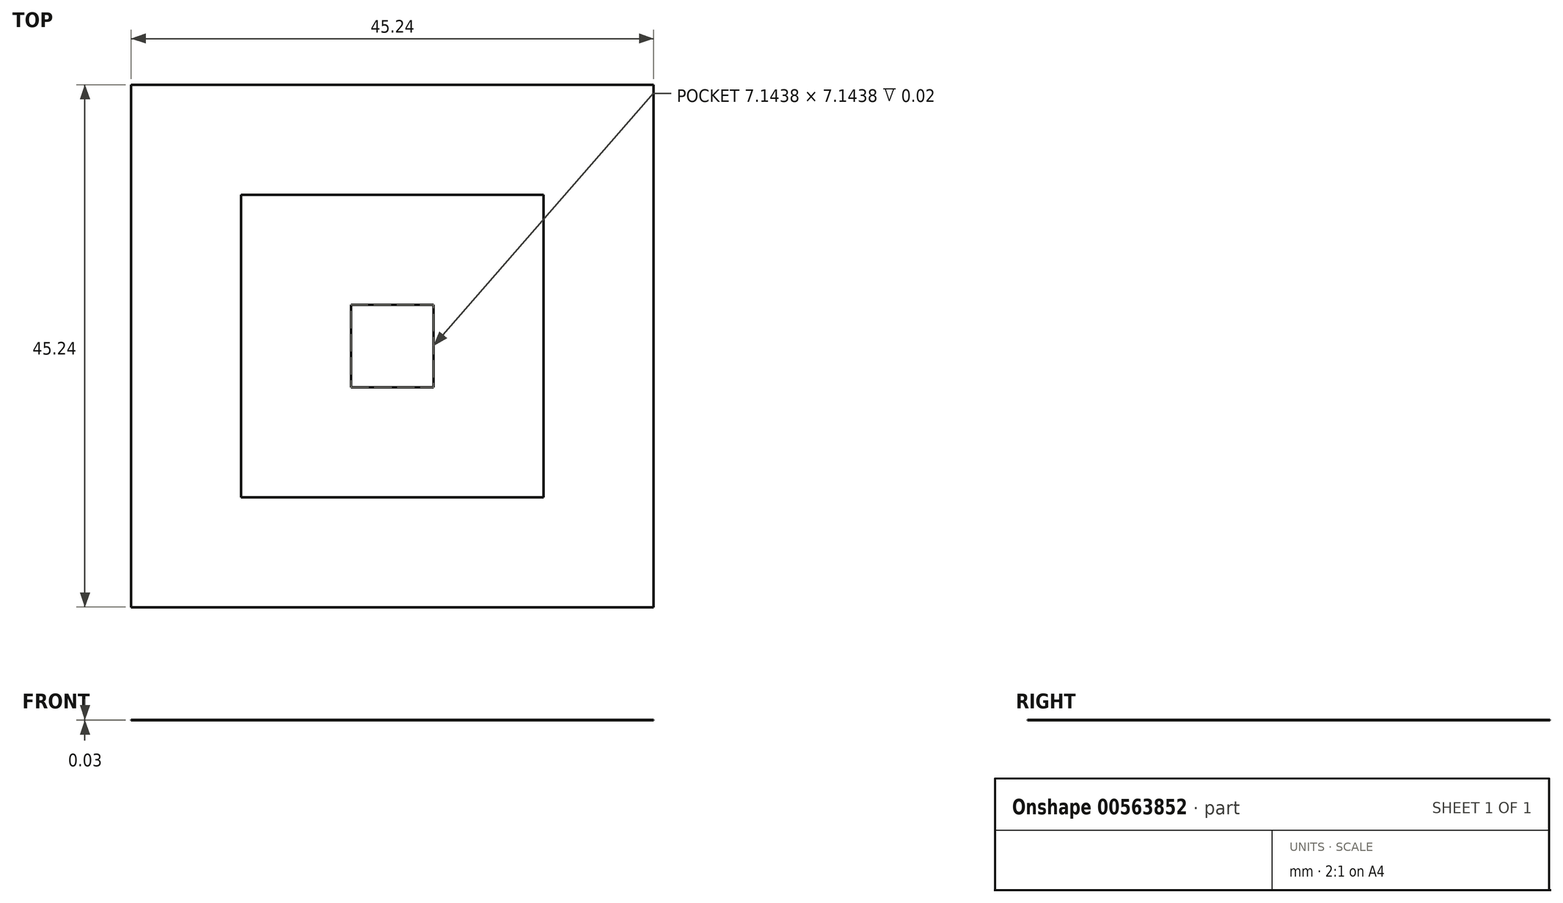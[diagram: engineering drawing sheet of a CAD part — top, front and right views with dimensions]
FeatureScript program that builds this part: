
annotation { "Feature Type Name" : "Feature", "Feature Type Description" : "" }
export const myFeature = defineFeature(function(context is Context, id is Id, definition is map)
    precondition{}
    {
        {
            var Q0;
            Q0=qCreatedBy(makeId("Top.planeOp"),FACE);
            var sketch = newSketch(context, id + "F0", { "sketchPlane" : qUnion([Q0])});
            skLineSegment(sketch, "E0.bottom", {"start": v(3.57, 3.57) * mm, "end": v(-3.57, 3.57) * mm});
            skLineSegment(sketch, "E0.top", {"start": v(3.57, -3.57) * mm, "end": v(-3.57, -3.57) * mm});
            skLineSegment(sketch, "E0.left", {"start": v(3.57, 3.57) * mm, "end": v(3.57, -3.57) * mm});
            skLineSegment(sketch, "E0.right", {"start": v(-3.57, 3.57) * mm, "end": v(-3.57, -3.57) * mm});
            skPoint(sketch, "E0.middle", {"position": v(0, 0) * mm});
            skLineSegment(sketch, "E1.bottom", {"start": v(13.1, 13.1) * mm, "end": v(-13.1, 13.1) * mm});
            skLineSegment(sketch, "E1.top", {"start": v(13.1, -13.1) * mm, "end": v(-13.1, -13.1) * mm});
            skLineSegment(sketch, "E1.left", {"start": v(13.1, 13.1) * mm, "end": v(13.1, -13.1) * mm});
            skLineSegment(sketch, "E1.right", {"start": v(-13.1, 13.1) * mm, "end": v(-13.1, -13.1) * mm});
            skLineSegment(sketch, "E2.bottom", {"start": v(22.62, 22.62) * mm, "end": v(-22.62, 22.62) * mm});
            skLineSegment(sketch, "E2.top", {"start": v(22.62, -22.62) * mm, "end": v(-22.62, -22.62) * mm});
            skLineSegment(sketch, "E2.left", {"start": v(22.62, 22.62) * mm, "end": v(22.62, -22.62) * mm});
            skLineSegment(sketch, "E2.right", {"start": v(-22.62, 22.62) * mm, "end": v(-22.62, -22.62) * mm});
            skSolve(sketch);
        }
        {
            var Q0;
            Q0=makeQuery(id+"F0.imprint","IMPRINT",FACE,{"disambiguationData":[TD([[makeQuery(id+"F0.imprint","IMPRINT",EDGE,{"derivedFrom":sQuery(id+"F0.wireOp",EDGE,"E1.bottom")}),-1.0]])]});
            extrude(context, id + "F1", {"entities" : qUnion([Q0]), "depth" : 3 / 203.2 * mm, "offsetDistance" : 25.4 * mm});
        }
        {
            var Q0;
            Q0=makeQuery(id+"F0.imprint","IMPRINT",FACE,{"disambiguationData":[TD([[makeQuery(id+"F0.imprint","IMPRINT",EDGE,{"derivedFrom":sQuery(id+"F0.wireOp",EDGE,"E0.bottom")}),-1.0]])]});
            extrude(context, id + "F2", {"entities" : qUnion([Q0]), "operationType" : NewBodyOperationType.ADD, "depth" : 3 / 101.6 * mm, "offsetDistance" : 25.4 * mm});
        }
        {
            var Q0;
            Q0=makeQuery(id+"F0.imprint","IMPRINT",FACE,{"disambiguationData":[TD([[makeQuery(id+"F0.imprint","IMPRINT",EDGE,{"derivedFrom":sQuery(id+"F0.wireOp",EDGE,"E0.bottom")}),1.0]])]});
            extrude(context, id + "F3", {"entities" : qUnion([Q0]), "operationType" : NewBodyOperationType.ADD, "depth" : 1 / 101.6 * mm, "offsetDistance" : 25.4 * mm});
        }
    });
